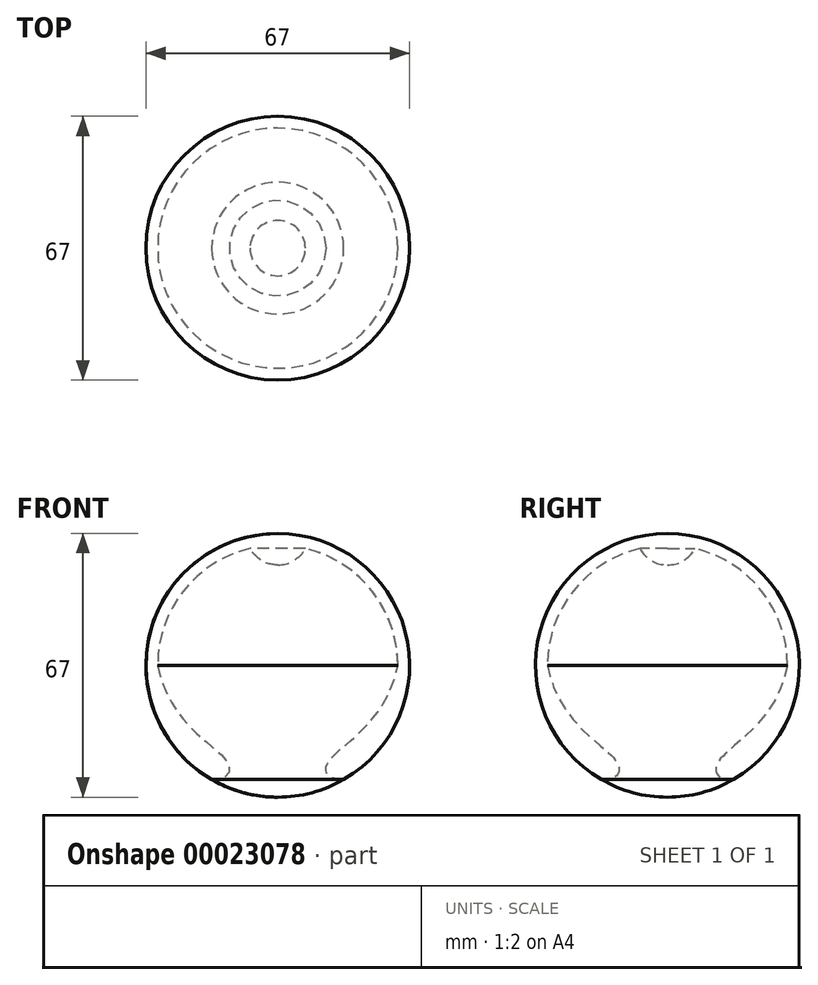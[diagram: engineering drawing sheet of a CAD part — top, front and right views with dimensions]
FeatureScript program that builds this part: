
annotation { "Feature Type Name" : "Feature", "Feature Type Description" : "" }
export const myFeature = defineFeature(function(context is Context, id is Id, definition is map)
    precondition{}
    {
        {
            var Q0;
            Q0=qCreatedBy(makeId("Front.planeOp"),FACE);
            var sketch = newSketch(context, id + "F0", { "sketchPlane" : qUnion([Q0])});
            skCircle(sketch, "E0", {"center": v(0, 0) * mm, "radius": 33.5 * mm, "construction": true});
            skArc(sketch, "E1", {"start": v(-7.03, 29.68) * mm, "mid": v(-23.92, 18.92) * mm, "end": v(-30.5, 0) * mm});
            skLineSegment(sketch, "E2", {"start": v(0, 0) * mm, "end": v(-16.75, -29.01) * mm, "construction": true});
            skArc(sketch, "E3", {"start": v(-16.75, -29.01) * mm, "mid": v(-13.12, -28.53) * mm, "end": v(-12.66, -24.9) * mm, "construction": true});
            skArc(sketch, "E4", {"start": v(-16.75, -29.01) * mm, "mid": v(-8.67, -32.36) * mm, "end": v(0, -33.5) * mm});
            skPoint(sketch, "E5", {"position": v(0, -33.5) * mm});
            skPoint(sketch, "E6.end.orphan", {"position": v(16.75, -29.01) * mm});
            skArc(sketch, "E7", {"start": v(0, 33.5) * mm, "mid": v(-32.36, 8.67) * mm, "end": v(-16.75, -29.01) * mm});
            skFitSpline(sketch, "E8", {"points": [v(-16.75, -29.01) * mm, v(-12.66, -24.9) * mm, v(-30.5, 0) * mm], "startDerivative": vector(43.62, 0) * mm, "endDerivative": vector(-13.61, 67.71) * mm});
            skLineSegment(sketch, "E9", {"start": v(0, 33.5) * mm, "end": v(0, -33.5) * mm});
            skPoint(sketch, "E10", {"position": v(-33.5, 0) * mm});
            skArc(sketch, "E11", {"start": v(-7.03, 29.68) * mm, "mid": v(-4.09, 26.62) * mm, "end": v(0, 25.5) * mm});
            skLineSegment(sketch, "E12", {"start": v(-34.88, -29.01) * mm, "end": v(-16.75, -29.01) * mm, "construction": true});
            skSolve(sketch);
        }
        {
            var Q0;
            Q0=makeQuery(id+"F0.imprint","IMPRINT",FACE,{"disambiguationData":[TD([[makeQuery(id+"F0.imprint","IMPRINT",EDGE,{"derivedFrom":sQuery(id+"F0.wireOp",EDGE,"E1")}),1.0]])]});
            var Q1;
            Q1=sQuery(id+"F0.wireOp",EDGE,"E9");
            revolve(context, id + "F1", {"entities" : qUnion([Q0]), "axis" : qUnion([Q1]), "revolveType" : RevolveType.FULL});
        }
        {
            var Q0;
            Q0=makeQuery(id+"F0.imprint","IMPRINT",FACE,{"disambiguationData":[TD([[makeQuery(id+"F0.imprint","IMPRINT",EDGE,{"derivedFrom":sQuery(id+"F0.wireOp",EDGE,"E1")}),-1.0]])]});
            var Q1;
            Q1=sQuery(id+"F0.wireOp",EDGE,"E9");
            revolve(context, id + "F2", {"entities" : qUnion([Q0]), "axis" : qUnion([Q1]), "revolveType" : RevolveType.FULL});
        }
    });
